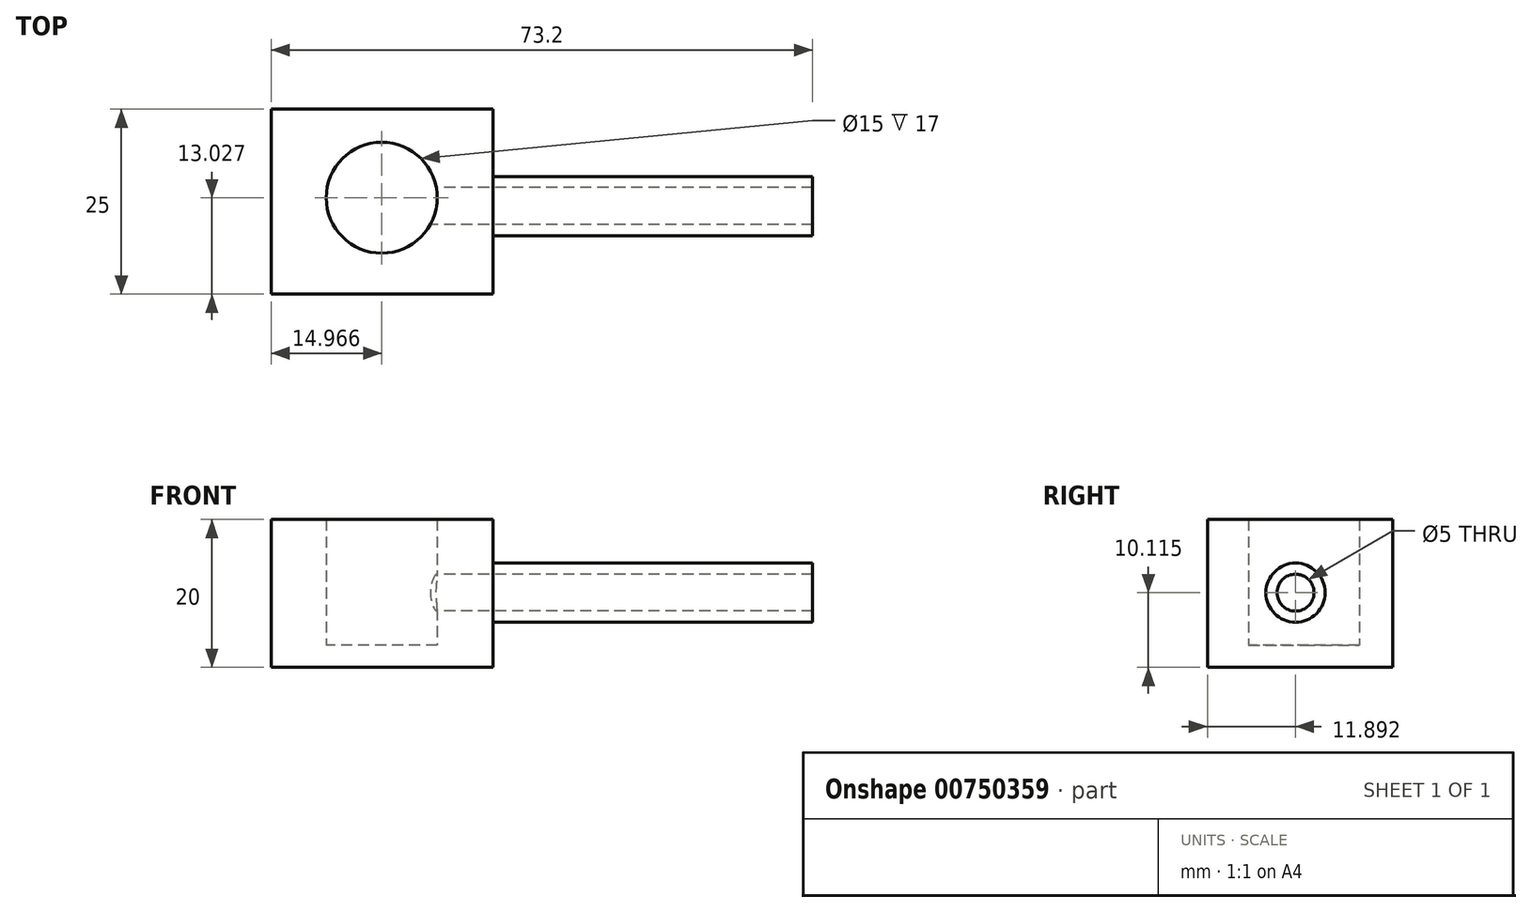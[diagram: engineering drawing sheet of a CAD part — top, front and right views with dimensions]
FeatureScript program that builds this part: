
annotation { "Feature Type Name" : "Feature", "Feature Type Description" : "" }
export const myFeature = defineFeature(function(context is Context, id is Id, definition is map)
    precondition{}
    {
        {
            var Q0;
            Q0=qCreatedBy(makeId("Front.planeOp"),FACE);
            var sketch = newSketch(context, id + "F0", { "sketchPlane" : qUnion([Q0])});
            skLineSegment(sketch, "E0.bottom", {"start": v(0, 0) * mm, "end": v(30, 0) * mm});
            skLineSegment(sketch, "E0.top", {"start": v(0, 20) * mm, "end": v(30, 20) * mm});
            skLineSegment(sketch, "E0.left", {"start": v(0, 0) * mm, "end": v(0, 20) * mm});
            skLineSegment(sketch, "E0.right", {"start": v(30, 0) * mm, "end": v(30, 20) * mm});
            skSolve(sketch);
        }
        {
            var Q0;
            Q0 = qSketchRegion(id + "F0", true);
            extrude(context, id + "F1", {"entities" : qUnion([Q0]), "depth" : 25 * mm, "offsetDistance" : 25 * mm});
        }
        {
            var Q0;
            Q0=qCreatedBy(makeId("Top.planeOp"),FACE);
            var sketch = newSketch(context, id + "F2", { "sketchPlane" : qUnion([Q0])});
            skCircle(sketch, "E1", {"center": v(14.97, -11.97) * mm, "radius": 7.5 * mm});
            skSolve(sketch);
        }
        {
            var Q0;
            Q0 = qSketchRegion(id + "F2", true);
            extrude(context, id + "F3", {"entities" : qUnion([Q0]), "operationType" : NewBodyOperationType.REMOVE, "depth" : 26 * mm, "offsetDistance" : 25 * mm});
        }
        {
            var Q0;
            Q0=qCreatedBy(makeId("Top.planeOp"),FACE);
            var sketch = newSketch(context, id + "F4", { "sketchPlane" : qUnion([Q0])});
            skLineSegment(sketch, "E2.bottom", {"start": v(0, 0) * mm, "end": v(30, 0) * mm});
            skLineSegment(sketch, "E2.top", {"start": v(0, -25) * mm, "end": v(30, -25) * mm});
            skLineSegment(sketch, "E2.left", {"start": v(0, 0) * mm, "end": v(0, -25) * mm});
            skLineSegment(sketch, "E2.right", {"start": v(30, 0) * mm, "end": v(30, -25) * mm});
            skSolve(sketch);
        }
        {
            var Q0;
            Q0 = qSketchRegion(id + "F4", true);
            extrude(context, id + "F5", {"entities" : qUnion([Q0]), "operationType" : NewBodyOperationType.ADD, "depth" : 3 * mm, "offsetDistance" : 25 * mm});
        }
        {
            var Q0;
            Q0=qCreatedBy(makeId("Right.planeOp"),FACE);
            var sketch = newSketch(context, id + "F6", { "sketchPlane" : qUnion([Q0])});
            skCircle(sketch, "E3", {"center": v(-13.1, 10.11) * mm, "radius": 2.5 * mm});
            skSolve(sketch);
        }
        {
            var Q0;
            Q0=qCreatedBy(makeId("Right.planeOp"),FACE);
            var sketch = newSketch(context, id + "F7", { "sketchPlane" : qUnion([Q0])});
            skCircle(sketch, "E4", {"center": v(-13.1, 10.11) * mm, "radius": 4 * mm});
            skSolve(sketch);
        }
        {
            var Q0;
            Q0 = qSketchRegion(id + "F7", true);
            extrude(context, id + "F8", {"entities" : qUnion([Q0]), "operationType" : NewBodyOperationType.ADD, "depth" : 73.2 * mm, "offsetDistance" : 25 * mm, "hasSecondDirection" : true, "secondDirectionOppositeDirection" : false, "secondDirectionDepth" : 25.6 * mm});
        }
        {
            var Q0;
            Q0 = qSketchRegion(id + "F6", true);
            extrude(context, id + "F9", {"entities" : qUnion([Q0]), "operationType" : NewBodyOperationType.REMOVE, "depth" : 88.2 * mm, "offsetDistance" : 25 * mm, "hasSecondDirection" : true, "secondDirectionOppositeDirection" : false, "secondDirectionDepth" : 17.7 * mm});
        }
    });
